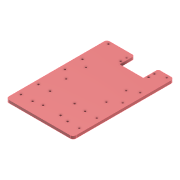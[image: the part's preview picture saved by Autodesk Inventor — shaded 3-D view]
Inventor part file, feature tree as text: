
AUTODESK INVENTOR PART (.ipt)
format: ipt  version: 2022 (Build 260153000, 153)  size: 258,048 bytes
history: native  units: mm
features: sketch x9, hole x8, extrude x2, fillet x2, other x1, projected_geometry x1
ambient origin geometry x8: Origin, YZ Plane, XZ Plane, XY Plane, X Axis, Y Axis, Z Axis, Center Point
bodies: Solid1 (feature_tree)
feature tree (23):
  extrude  "Base"  TaperAngle=0.0deg  [1 undecoded]
  hole  "Bearing Holder Mounting Holes"  [1 undecoded]
  fillet  "Fillet1"  Radius=18.0mm
  hole  "12v Motor Mount Mounting Holes"  [1 undecoded]
  extrude  "Servo Cutout 2"  Depth=10.0mm
  hole  "Servo Mounting Holes 2"  [1 undecoded]
  hole  "Extra Holes For Top Plate"  [1 undecoded]
  hole  "Ultrasonic Sensor Mounting Holes"  [1 undecoded]
  other  "Clearance for Servo"
  hole  "Driver Gear Stopper Mounting Holes"  [1 undecoded]
  fillet  "Fillet2"  [1 undecoded]
  hole  "Optical sensor holes"  [1 undecoded]
  hole  "CounterBore for Bearing Holder Mounting Holes"  [1 undecoded]
  sketch  "Sketch2"  dims[d2=115.0mm d4=0.0mm]
  sketch  "Sketch5"  dims[d5=20.0mm d6=30.0mm d8=18.0mm]
  sketch  "Sketch8"  dims[d9=3.4mm d10=6.0mm d11=4.0mm d12=2.0mm d13=90.0deg d14=8.0mm d15=20.594885mm d16=10.0mm]
  sketch  "Sketch9"  dims[d18=20.0mm d19=10.0mm]
  sketch  "Sketch10"  dims[d20=50.0mm d21=5.0mm]
  sketch  "Sketch11"  dims[d41=34.0mm d42=69.0mm]
  sketch  "Sketch13"  dims[d43=80.0mm]
  sketch  "Sketch15"  dims[d44=3.2mm d45=6.0mm d46=4.0mm d47=2.0mm d48=90.0deg d49=8.0mm d50=20.594885mm d64=20.0mm]
  sketch  "Sketch16"  dims[d65=40.0mm d67=10.0mm d68=0.0mm d69=0.0mm d70=3.925mm d71=5.0mm d72=3.925mm d73=3.4mm d74=6.0mm d75=4.0mm d76=2.0mm d77=90.0deg d78=8.0mm d79=20.594885mm d84=3.4mm d85=6.0mm d86=4.0mm d87=2.0mm d88=90.0deg d89=6.0mm d90=0.0mm d93=5.0mm d94=50.0mm d95=50.0mm d96=30.0mm d97=8.0mm d98=3.4mm d99=6.0mm d100=7.0mm d101=2.0mm d102=90.0deg d103=6.0mm d104=0.0mm d105=0.5mm d106=0.2mm d108=30.0mm d110=8.0mm d111=50.0mm d123=30.0mm d124=60.5mm d125=3.4mm d126=6.0mm d127=7.0mm d128=2.0mm d129=90.0deg d130=8.0mm d131=20.594885mm d139=7.0mm d140=6.0mm d141=6.0mm d142=2.0mm d143=90.0deg d144=2.0mm d145=0.0mm d146=21.0mm d147=5.0mm d148=3.0mm d149=13.0mm d150=15.0mm d151=7.0mm d152=8.0mm d153=8.0mm d156=3.4mm d157=6.0mm d158=4.0mm d159=2.0mm d160=90.0deg d161=8.0mm d162=20.594885mm d163=12.0mm d164=6.0mm]
  projected_geometry  "Project Cut Edges1"
note: 10 required parameter values undecoded (feature->parameter linkage not recoverable at this tier; creation-order binding heuristic only, values carry confidence <= 0.55)
